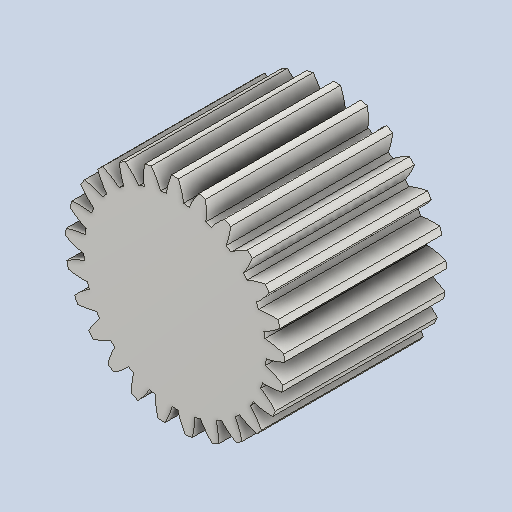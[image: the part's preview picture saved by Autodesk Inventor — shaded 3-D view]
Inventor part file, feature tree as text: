
AUTODESK INVENTOR PART (.ipt)
format: ipt  version: 2024 (Build 280153000, 153)  size: 286,208 bytes
history: native  units: mm (DEFAULTED — no unit token found)
features: plane x3, other x3, extrude x1, sketch x1
ambient origin geometry x8: Origin, YZ Plane, XZ Plane, XY Plane, X Axis, Y Axis, Z Axis, Center Point
bodies: Solid1 (feature_tree)
feature tree (8):
  extrude  "Extrusion1"  Depth=40.0mm TaperAngle=0.0deg
  plane  "Work Plane2"
  plane  "Work Plane8"
  plane  "Work Plane9"
  other  "Spur Gear"
  sketch  "Sketch1"  dims[d0=54.0mm d1=40.0mm d2=0.0mm d3=50.0mm d4=10.0mm d5=0.0mm d16=35.0mm d17=0.0mm d34=1.256637mm d39=0.0mm d41=0.0mm d43=35.0mm d46=35.0mm d47=0.0mm d48=0.0mm]
  other  "Srf1"
  other  "Pitch Diameter"
